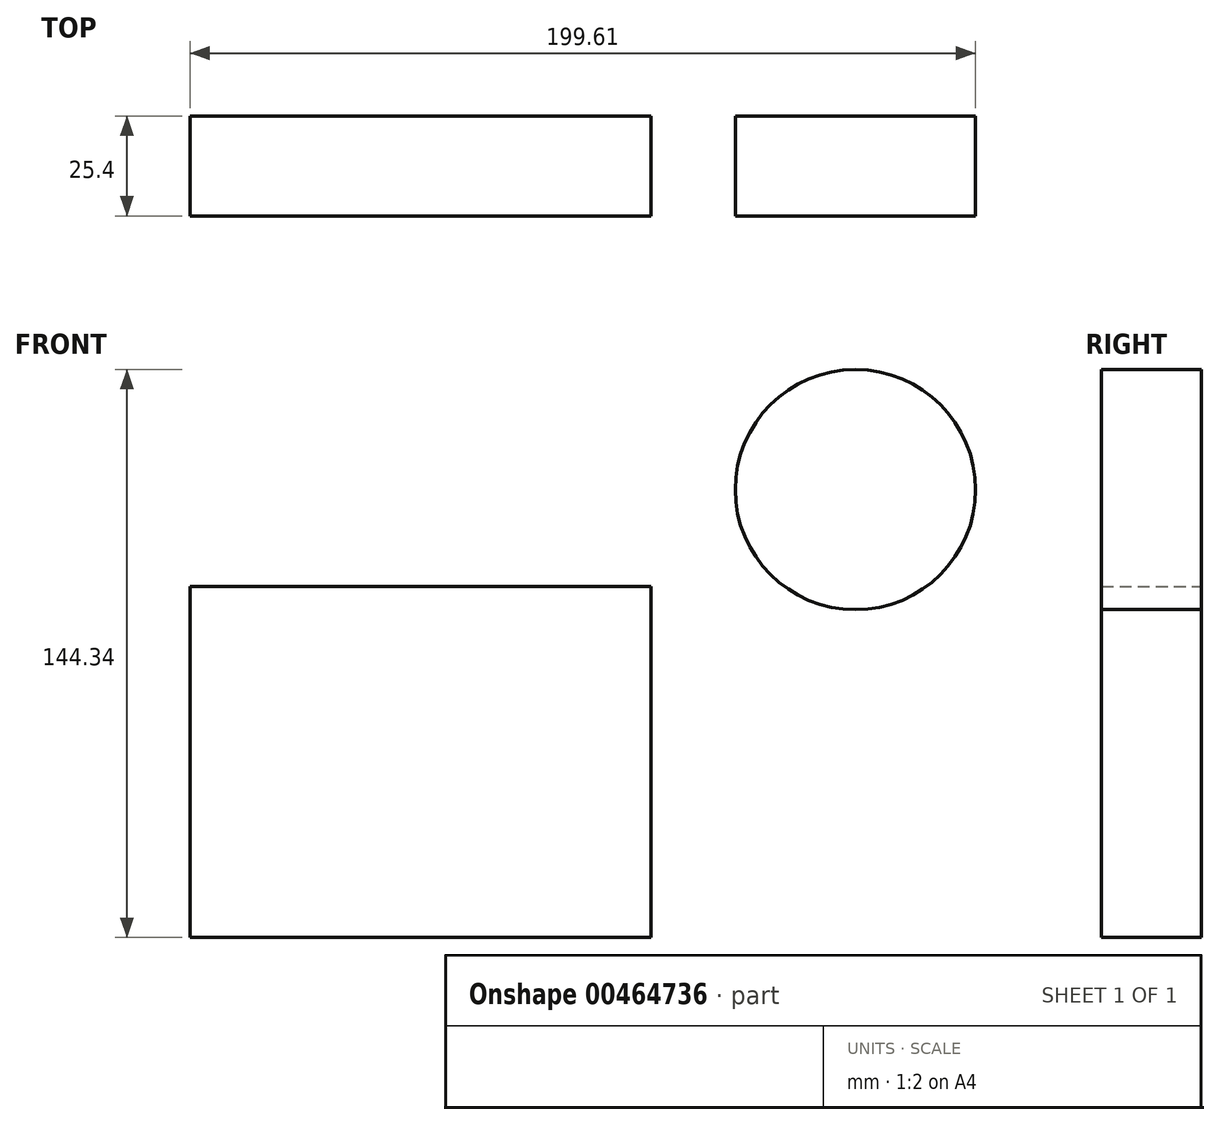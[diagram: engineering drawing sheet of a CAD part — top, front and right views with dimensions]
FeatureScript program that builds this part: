
annotation { "Feature Type Name" : "Feature", "Feature Type Description" : "" }
export const myFeature = defineFeature(function(context is Context, id is Id, definition is map)
    precondition{}
    {
        {
            var Q0;
            Q0=qCreatedBy(makeId("Front.planeOp"),FACE);
            var sketch = newSketch(context, id + "F0", { "sketchPlane" : qUnion([Q0])});
            skLineSegment(sketch, "E0.bottom", {"start": v(-12.04, 44.6) * mm, "end": v(-129.14, 44.6) * mm});
            skLineSegment(sketch, "E0.top", {"start": v(-12.04, -44.6) * mm, "end": v(-129.14, -44.6) * mm});
            skLineSegment(sketch, "E0.left", {"start": v(-12.04, 44.6) * mm, "end": v(-12.04, -44.6) * mm});
            skLineSegment(sketch, "E0.right", {"start": v(-129.14, 44.6) * mm, "end": v(-129.14, -44.6) * mm});
            skPoint(sketch, "E0.middle", {"position": v(-70.59, 0) * mm});
            skArc(sketch, "E1", {"start": v(-12.04, 44.6) * mm, "mid": v(6.16, 73.36) * mm, "end": v(39.94, 69.22) * mm});
            skCircle(sketch, "E2", {"center": v(39.94, 69.22) * mm, "radius": 30.53 * mm});
            skSolve(sketch);
        }
        {
            var Q0;
            Q0 = qSketchRegion(id + "F0", true);
            extrude(context, id + "F1", {"entities" : qUnion([Q0]), "depth" : 25.4 * mm});
        }
    });
